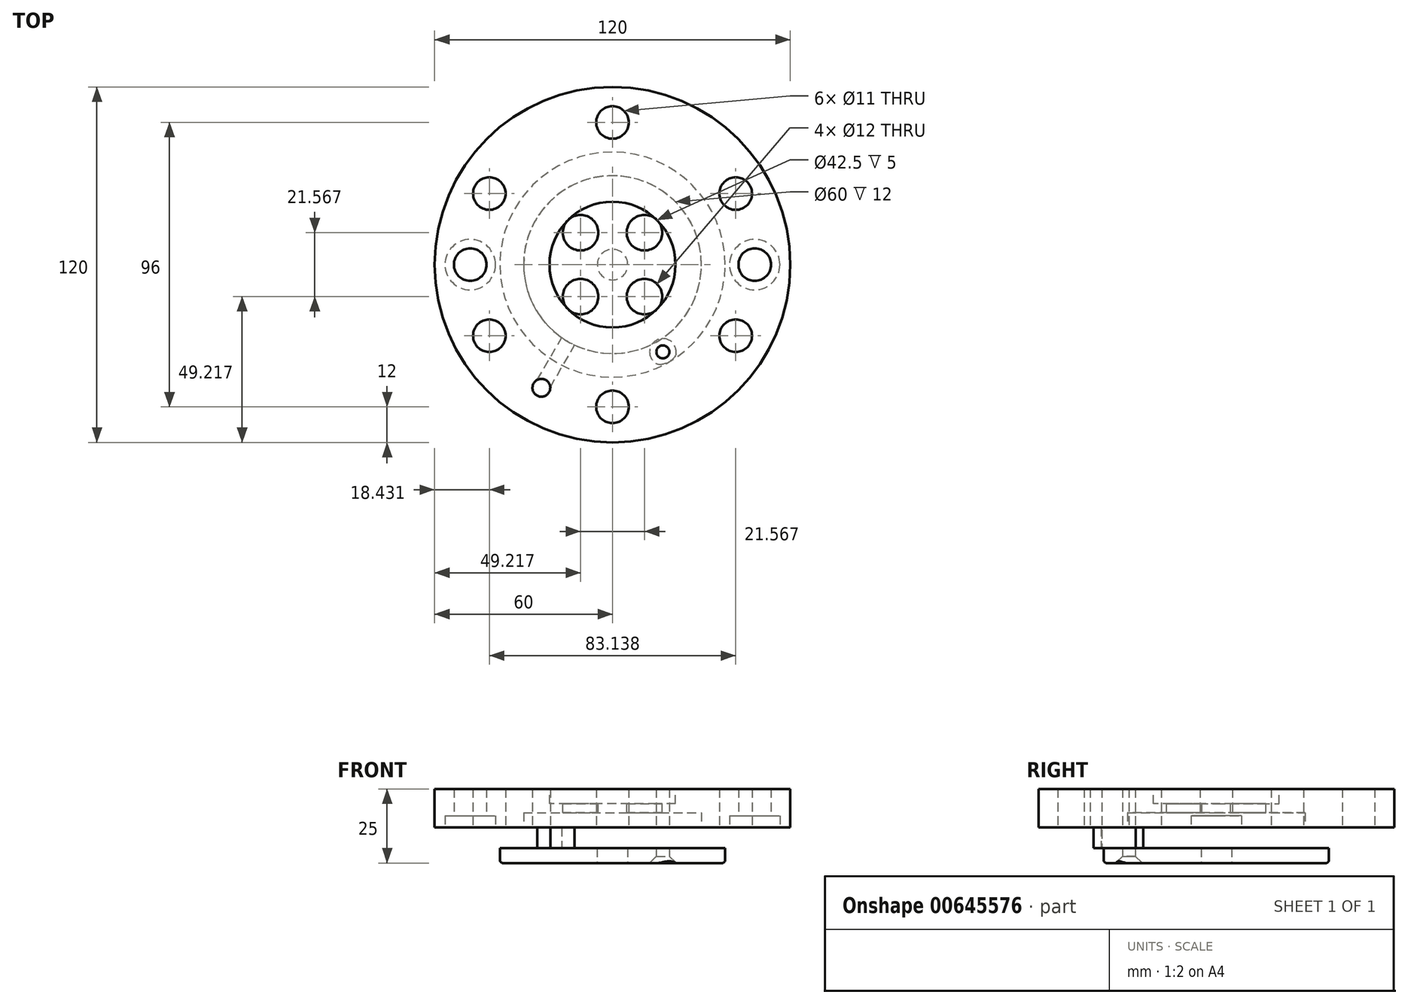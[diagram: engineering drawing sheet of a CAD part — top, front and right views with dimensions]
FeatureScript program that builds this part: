
annotation { "Feature Type Name" : "Feature", "Feature Type Description" : "" }
export const myFeature = defineFeature(function(context is Context, id is Id, definition is map)
    precondition{}
    {
        {
            var Q0;
            Q0=qCreatedBy(makeId("Top.planeOp"),FACE);
            var sketch = newSketch(context, id + "F0", { "sketchPlane" : qUnion([Q0])});
            skCircle(sketch, "E0", {"center": v(0, 0) * mm, "radius": 60 * mm});
            skSolve(sketch);
        }
        {
            var Q0;
            Q0 = qSketchRegion(id + "F0", true);
            extrude(context, id + "F1", {"entities" : qUnion([Q0]), "depth" : 20 * mm, "offsetDistance" : 25 * mm});
        }
        {
            var Q0;
            Q0=makeQuery(id+"F1.opExtrude","CAP_FACE",FACE,{"disambiguationData":[OSD([sQuery(id+"F0.wireOp",EDGE,"E0")])],"isStart":false});
            var sketch = newSketch(context, id + "F2", { "sketchPlane" : qUnion([Q0])});
            skCircle(sketch, "E1", {"center": v(0, 0) * mm, "radius": 21.25 * mm});
            skCircle(sketch, "E2.0", {"center": v(0, 0) * mm, "radius": 22.75 * mm});
            skSolve(sketch);
        }
        {
            var Q0;
            Q0=makeQuery(id+"F2.imprint","IMPRINT",FACE,{"disambiguationData":[TD([[makeQuery(id+"F2.imprint","IMPRINT",EDGE,{"derivedFrom":sQuery(id+"F2.wireOp",EDGE,"E1")}),1.0]])]});
            extrude(context, id + "F3", {"entities" : qUnion([Q0]), "operationType" : NewBodyOperationType.REMOVE, "oppositeDirection" : true, "depth" : 5 * mm, "offsetDistance" : 25 * mm});
        }
        {
            var Q0;
            Q0=makeQuery(id+"F2.imprint","IMPRINT",FACE,{"disambiguationData":[TD([[makeQuery(id+"F2.imprint","IMPRINT",EDGE,{"derivedFrom":sQuery(id+"F2.wireOp",EDGE,"E1")}),1.0]])]});
            var sketch = newSketch(context, id + "F4", { "sketchPlane" : qUnion([Q0])});
            skCircle(sketch, "E3", {"center": v(10.78, 10.78) * mm, "radius": 6 * mm});
            skLineSegment(sketch, "E4", {"start": v(0, 0) * mm, "end": v(22.1, 22.1) * mm, "construction": true});
            skCircle(sketch, "E5.1.0", {"center": v(-10.78, 10.78) * mm, "radius": 6 * mm});
            skCircle(sketch, "E5.2.0", {"center": v(-10.78, -10.78) * mm, "radius": 6 * mm});
            skPoint(sketch, "E5.center", {"position": v(0, 0) * mm});
            skCircle(sketch, "E6.1.3.0", {"center": v(10.78, -10.78) * mm, "radius": 6 * mm});
            skSolve(sketch);
        }
        {
            var Q0;
            Q0 = qSketchRegion(id + "F4", true);
            extrude(context, id + "F5", {"entities" : qUnion([Q0]), "operationType" : NewBodyOperationType.REMOVE, "endBound" : BoundingType.THROUGH_ALL, "oppositeDirection" : true, "depth" : 25 * mm, "offsetDistance" : 25 * mm});
        }
        {
            var Q0;
            Q0=makeQuery(id+"F1.opExtrude","CAP_FACE",FACE,{"disambiguationData":[OSD([sQuery(id+"F0.wireOp",EDGE,"E0")])],"isStart":true});
            var sketch = newSketch(context, id + "F6", { "sketchPlane" : qUnion([Q0])});
            skCircle(sketch, "E7.0", {"center": v(0, 0) * mm, "radius": 30 * mm});
            skSolve(sketch);
        }
        {
            var Q0;
            Q0 = qSketchRegion(id + "F6", true);
            extrude(context, id + "F7", {"entities" : qUnion([Q0]), "operationType" : NewBodyOperationType.REMOVE, "oppositeDirection" : true, "depth" : 12 * mm, "offsetDistance" : 25 * mm});
        }
        {
            var Q0;
            Q0=makeQuery(id+"F1.opExtrude","CAP_FACE",FACE,{"disambiguationData":[OSD([sQuery(id+"F0.wireOp",EDGE,"E0")])],"isStart":true});
            var sketch = newSketch(context, id + "F8", { "sketchPlane" : qUnion([Q0])});
            skCircle(sketch, "E8", {"center": v(-48, 0) * mm, "radius": 8.5 * mm});
            skCircle(sketch, "E9.MirrorC", {"center": v(48, 0) * mm, "radius": 8.5 * mm});
            skSolve(sketch);
        }
        {
            var Q0;
            Q0 = qSketchRegion(id + "F8", true);
            extrude(context, id + "F9", {"entities" : qUnion([Q0]), "operationType" : NewBodyOperationType.REMOVE, "oppositeDirection" : true, "depth" : 11 * mm, "offsetDistance" : 25 * mm});
        }
        {
            var Q0;
            Q0=makeQuery(id+"F9.boolean.opBoolean","COPY",FACE,{"derivedFrom":makeQuery(id+"F9.opExtrude","CAP_FACE",FACE,{"disambiguationData":[OSD([sQuery(id+"F8.wireOp",EDGE,"E8")])],"isStart":false})});
            var sketch = newSketch(context, id + "F10", { "sketchPlane" : qUnion([Q0])});
            skCircle(sketch, "E10", {"center": v(-48, 0) * mm, "radius": 5.5 * mm});
            skCircle(sketch, "E11.MirrorC", {"center": v(48, 0) * mm, "radius": 5.5 * mm});
            skSolve(sketch);
        }
        {
            var Q0;
            Q0 = qSketchRegion(id + "F10", true);
            extrude(context, id + "F11", {"entities" : qUnion([Q0]), "operationType" : NewBodyOperationType.REMOVE, "endBound" : BoundingType.THROUGH_ALL, "oppositeDirection" : true, "depth" : 25 * mm, "offsetDistance" : 25 * mm});
        }
        {
            var Q0;
            Q0=makeQuery(id+"F1.opExtrude","CAP_FACE",FACE,{"disambiguationData":[OSD([sQuery(id+"F0.wireOp",EDGE,"E0")])],"isStart":true});
            var sketch = newSketch(context, id + "F12", { "sketchPlane" : qUnion([Q0])});
            skCircle(sketch, "E12", {"center": v(41.57, 24) * mm, "radius": 5.5 * mm});
            skLineSegment(sketch, "E13", {"start": v(0, 0) * mm, "end": v(56.15, 32.42) * mm, "construction": true});
            skCircle(sketch, "E14.1.0", {"center": v(0, 48) * mm, "radius": 5.5 * mm});
            skCircle(sketch, "E14.2.0", {"center": v(-41.57, 24) * mm, "radius": 5.5 * mm});
            skCircle(sketch, "E14.3.0", {"center": v(-41.57, -24) * mm, "radius": 5.5 * mm});
            skCircle(sketch, "E14.4.0", {"center": v(0, -48) * mm, "radius": 5.5 * mm});
            skCircle(sketch, "E14.5.0", {"center": v(41.57, -24) * mm, "radius": 5.5 * mm});
            skPoint(sketch, "E14.center", {"position": v(0, 0) * mm});
            skSolve(sketch);
        }
        {
            var Q0;
            Q0 = qSketchRegion(id + "F12", true);
            extrude(context, id + "F13", {"entities" : qUnion([Q0]), "operationType" : NewBodyOperationType.REMOVE, "endBound" : BoundingType.THROUGH_ALL, "oppositeDirection" : true, "depth" : 25 * mm, "offsetDistance" : 25 * mm});
        }
        {
            var Q0;
            Q0=makeQuery(id+"F1.opExtrude","CAP_FACE",FACE,{"disambiguationData":[OSD([sQuery(id+"F0.wireOp",EDGE,"E0")])],"isStart":true});
            var sketch = newSketch(context, id + "F14", { "sketchPlane" : qUnion([Q0])});
            skPoint(sketch, "E15", {"position": v(17, 29.44) * mm});
            skLineSegment(sketch, "E16", {"start": v(0, 0) * mm, "end": v(-21.03, 36.43) * mm, "construction": true});
            skLineSegment(sketch, "E17", {"start": v(0, 0) * mm, "end": v(25.5, 44.17) * mm, "construction": true});
            skSolve(sketch);
        }
        {
            var Q0;
            Q0=sQuery(id+"F14.wireOp",VERTEX,"E15");
            var Q1;
            Q1=makeQuery(id+"F1.opExtrude","SWEPT_BODY",BODY,{"disambiguationData":[OSD([sQuery(id+"F0.wireOp",EDGE,"E0")])]});
            hole(context, id + "F15", {"style" : HoleStyle.SIMPLE, "endStyle" : HoleEndStyle.THROUGH, "standardTappedOrClearance" : lookupTablePath({ "standard" : "ISO", "fit" : "Normal", "size" : "M4", "type" : "Clearance" }), "standardBlindInLast" : lookupTablePath({ "fit" : "Standard", "standard" : "ISO", "size" : "M4", "type" : "Clearance" }), "holeDiameter" : 4.4 * mm, "majorDiameter" : 5 * mm, "tappedDepth" : 15 * mm, "tapClearance" : 3, "locations" : qUnion([Q0]), "scope" : qUnion([Q1])});
        }
        {
            var Q0;
            Q0=makeQuery(id+"F1.opExtrude","CAP_FACE",FACE,{"disambiguationData":[OSD([sQuery(id+"F0.wireOp",EDGE,"E0")])],"isStart":true});
            var sketch = newSketch(context, id + "F16", { "sketchPlane" : qUnion([Q0])});
            skCircle(sketch, "E18", {"center": v(0, 0) * mm, "radius": 38 * mm});
            skSolve(sketch);
        }
        {
            var Q0;
            Q0 = qSketchRegion(id + "F16", true);
            extrude(context, id + "F17", {"entities" : qUnion([Q0]), "depth" : 5 * mm, "offsetDistance" : 25 * mm});
        }
        {
            var Q0;
            Q0=makeQuery(id+"F17.opExtrude","CAP_FACE",FACE,{"disambiguationData":[OSD([sQuery(id+"F16.wireOp",EDGE,"E18")])],"isStart":false});
            var sketch = newSketch(context, id + "F18", { "sketchPlane" : qUnion([Q0])});
            skPoint(sketch, "E19.0", {"position": v(17, 29.44) * mm});
            skSolve(sketch);
        }
        {
            var Q0;
            Q0=sQuery(id+"F18.wireOp",VERTEX,"E19.0");
            var Q1;
            Q1=makeQuery(id+"F17.opExtrude","SWEPT_BODY",BODY,{"disambiguationData":[OSD([sQuery(id+"F16.wireOp",EDGE,"E18")])]});
            hole(context, id + "F19", {"style" : HoleStyle.C_SINK, "endStyle" : HoleEndStyle.THROUGH, "standardTappedOrClearance" : lookupTablePath({ "standard" : "ISO", "fit" : "Normal", "size" : "M4", "type" : "Clearance" }), "standardBlindInLast" : lookupTablePath({ "fit" : "Standard", "standard" : "ISO", "size" : "M4", "type" : "Clearance" }), "holeDiameter" : 4.4 * mm, "cSinkDiameter" : 8.96 * mm, "cSinkAngle" : 90 * degree, "majorDiameter" : 5 * mm, "tappedDepth" : 15 * mm, "tapClearance" : 3, "locations" : qUnion([Q0]), "scope" : qUnion([Q1])});
        }
        {
            var Q0;
            Q0=makeQuery(id+"FmNCdzJL0xRl9PW_2.1.F19.hole-0.boolean.opBoolean","SPLIT",EDGE,{"disambiguationData":[OD(0.0)],"derivedFrom":makeQuery(id+"F17.opExtrude","CAP_EDGE",EDGE,{"disambiguationData":[OSD([sQuery(id+"F16.wireOp",EDGE,"E18")])],"isStart":false})});
            fillet(context, id + "F20", {"entities" : qUnion([Q0]), "radius" : 1 * mm, "tangentPropagation" : true, "allowEdgeOverflow" : false});
        }
        {
            var Q0;
            Q0=makeQuery(id+"F17.opExtrude","CAP_FACE",FACE,{"disambiguationData":[OSD([sQuery(id+"F16.wireOp",EDGE,"E18")])],"isStart":false});
            var sketch = newSketch(context, id + "F21", { "sketchPlane" : qUnion([Q0])});
            skPoint(sketch, "E20", {"position": v(0, 0) * mm});
            skSolve(sketch);
        }
        {
            var Q0;
            Q0=sQuery(id+"F21.wireOp",VERTEX,"E20");
            var Q1;
            Q1=makeQuery(id+"F17.opExtrude","SWEPT_BODY",BODY,{"disambiguationData":[OSD([sQuery(id+"F16.wireOp",EDGE,"E18")])]});
            hole(context, id + "F22", {"style" : HoleStyle.SIMPLE, "endStyle" : HoleEndStyle.BLIND, "standardTappedOrClearance" : lookupTablePath({ "standard" : "ISO", "engagement" : "75%", "pitch" : "1.75 mm", "size" : "M12", "type" : "Tapped" }), "standardBlindInLast" : lookupTablePath({ "standard" : "ISO", "engagement" : "75%", "pitch" : "1.75 mm", "size" : "M12", "type" : "Tapped" }), "holeDiameter" : 10.3 * mm, "majorDiameter" : 12 * mm, "showTappedDepth" : true, "holeDepth" : 20.25 * mm, "tappedDepth" : 15 * mm, "tapClearance" : 3, "locations" : qUnion([Q0]), "scope" : qUnion([Q1])});
        }
        {
            var Q0;
            Q0=makeQuery(id+"F14.imprint","IMPRINT",FACE,{"disambiguationData":[TD([[makeQuery(id+"F14.imprint","IMPRINT",EDGE,{"derivedFrom":makeQuery(id+"F1.opExtrude","CAP_EDGE",EDGE,{"disambiguationData":[OSD([sQuery(id+"F0.wireOp",EDGE,"E0")])],"isStart":true})}),-1.0]])]});
            var sketch = newSketch(context, id + "F23", { "sketchPlane" : qUnion([Q0])});
            skCircle(sketch, "E21", {"center": v(-24, 41.57) * mm, "radius": 3 * mm});
            skSolve(sketch);
        }
        {
            var Q0;
            Q0 = qSketchRegion(id + "F23", true);
            extrude(context, id + "F24", {"entities" : qUnion([Q0]), "operationType" : NewBodyOperationType.REMOVE, "oppositeDirection" : true, "depth" : 25 * mm, "offsetDistance" : 25 * mm});
        }
        {
            var Q0;
            Q0=makeQuery(id+"F14.imprint","IMPRINT",FACE,{"disambiguationData":[TD([[makeQuery(id+"F14.imprint","IMPRINT",EDGE,{"derivedFrom":makeQuery(id+"F1.opExtrude","CAP_EDGE",EDGE,{"disambiguationData":[OSD([sQuery(id+"F0.wireOp",EDGE,"E0")])],"isStart":true})}),-1.0]])]});
            var sketch = newSketch(context, id + "F25", { "sketchPlane" : qUnion([Q0])});
            skLineSegment(sketch, "E22", {"start": v(-24, 41.57) * mm, "end": v(-14.62, 25.32) * mm});
            skArc(sketch, "E23.0.startCap", {"start": v(-26.17, 40.32) * mm, "mid": v(-25.25, 43.73) * mm, "end": v(-21.83, 42.82) * mm});
            skArc(sketch, "E23.0.endCap", {"start": v(-12.45, 26.57) * mm, "mid": v(-13.37, 23.15) * mm, "end": v(-16.78, 24.07) * mm});
            skLineSegment(sketch, "E23.0.left", {"start": v(-21.83, 42.82) * mm, "end": v(-12.45, 26.57) * mm});
            skLineSegment(sketch, "E23.0.right", {"start": v(-26.17, 40.32) * mm, "end": v(-16.78, 24.07) * mm});
            skSolve(sketch);
        }
        {
            var Q0;
            {var subQ1=sQuery(id+"F25.wireOp",EDGE,"E23.0.startCap");Q0=makeQuery(id+"F25.imprint","IMPRINT",FACE,{"disambiguationData":[TD([[makeQuery(id+"F25.imprint","IMPRINT",EDGE,{"derivedFrom":subQ1}),-1.0]])]});}
            extrude(context, id + "F26", {"entities" : qUnion([Q0]), "operationType" : NewBodyOperationType.REMOVE, "oppositeDirection" : true, "depth" : 7 * mm, "offsetDistance" : 25 * mm});
        }
    });
